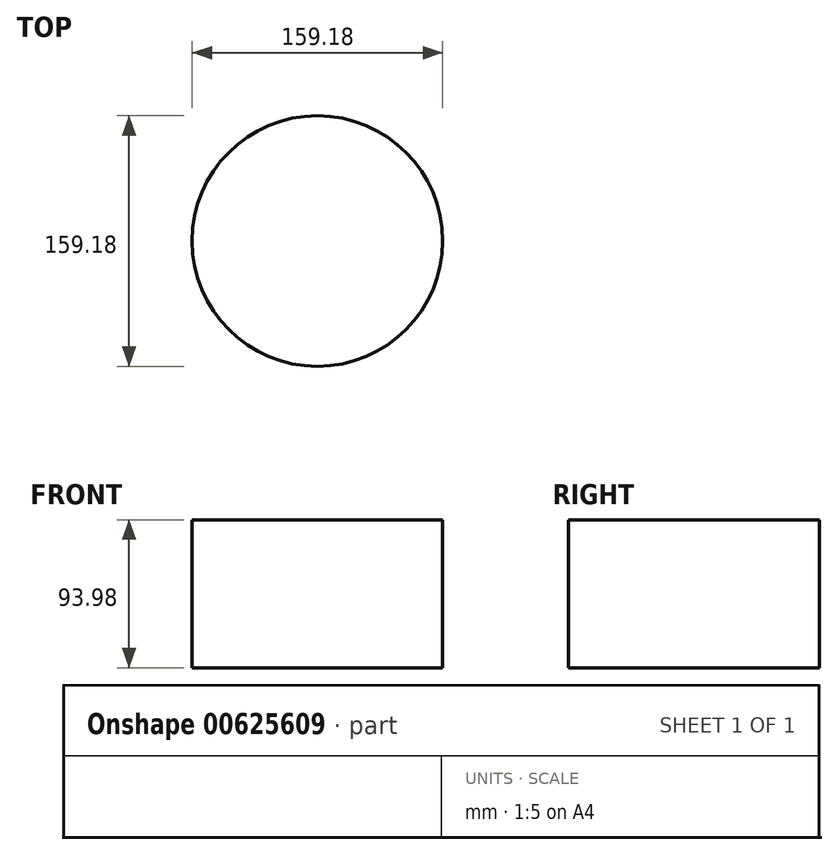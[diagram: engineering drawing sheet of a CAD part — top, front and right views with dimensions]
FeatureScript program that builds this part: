
annotation { "Feature Type Name" : "Feature", "Feature Type Description" : "" }
export const myFeature = defineFeature(function(context is Context, id is Id, definition is map)
    precondition{}
    {
        {
            var Q0;
            Q0=qCreatedBy(makeId("Top.planeOp"),FACE);
            var sketch = newSketch(context, id + "F0", { "sketchPlane" : qUnion([Q0])});
            skCircle(sketch, "E0", {"center": v(0, 0) * mm, "radius": 79.59 * mm});
            skSolve(sketch);
        }
        {
            var Q0;
            Q0=makeQuery(id+"F0.imprint","IMPRINT",FACE,{"disambiguationData":[TD([[makeQuery(id+"F0.imprint","IMPRINT",EDGE,{"derivedFrom":sQuery(id+"F0.wireOp",EDGE,"E0")}),1.0]])]});
            extrude(context, id + "F1", {"entities" : qUnion([Q0]), "depth" : 93.98 * mm, "offsetDistance" : 25.4 * mm});
        }
    });
